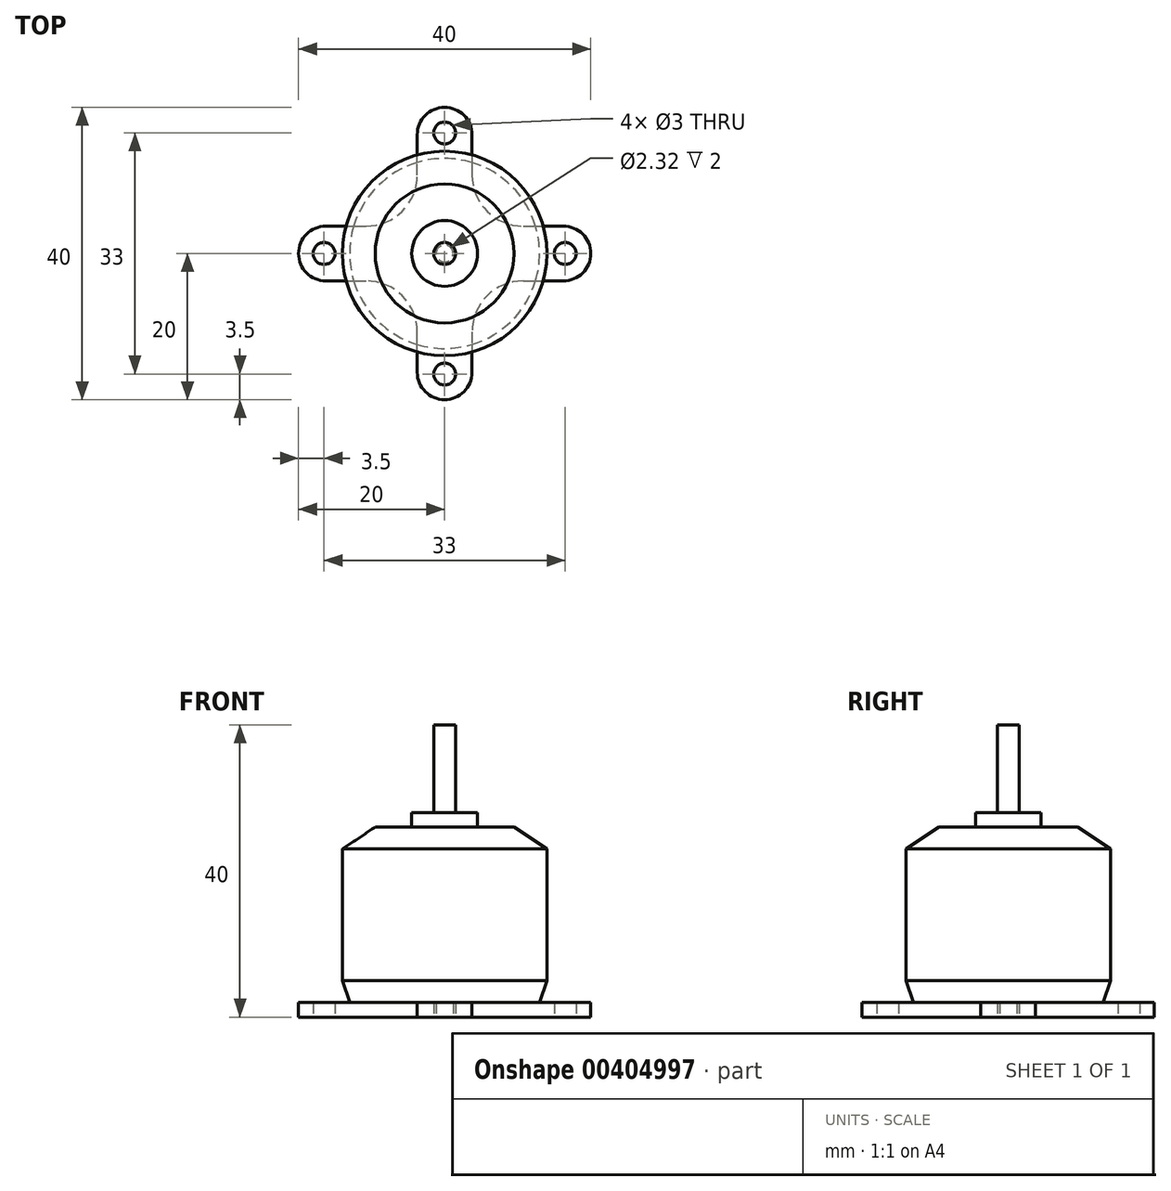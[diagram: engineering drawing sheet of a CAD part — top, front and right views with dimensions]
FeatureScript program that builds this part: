
annotation { "Feature Type Name" : "Feature", "Feature Type Description" : "" }
export const myFeature = defineFeature(function(context is Context, id is Id, definition is map)
    precondition{}
    {
        {
            var Q0;
            Q0=qCreatedBy(makeId("Front.planeOp"),FACE);
            var sketch = newSketch(context, id + "F0", { "sketchPlane" : qUnion([Q0])});
            skLineSegment(sketch, "E0", {"start": v(0, 0) * mm, "end": v(0, 40) * mm});
            skLineSegment(sketch, "E1", {"start": v(0, 40) * mm, "end": v(-1.5, 40) * mm});
            skLineSegment(sketch, "E2", {"start": v(-1.5, 40) * mm, "end": v(-1.5, 28) * mm});
            skLineSegment(sketch, "E3", {"start": v(-1.5, 28) * mm, "end": v(-4.5, 28) * mm});
            skLineSegment(sketch, "E4", {"start": v(-4.5, 28) * mm, "end": v(-4.5, 26) * mm});
            skLineSegment(sketch, "E5", {"start": v(-4.5, 26) * mm, "end": v(-9.5, 26) * mm});
            skLineSegment(sketch, "E6", {"start": v(-9.5, 26) * mm, "end": v(-14, 23) * mm});
            skLineSegment(sketch, "E7", {"start": v(-14, 23) * mm, "end": v(-14, 5) * mm});
            skLineSegment(sketch, "E8", {"start": v(-14, 5) * mm, "end": v(-13, 2) * mm});
            skLineSegment(sketch, "E9", {"start": v(-13, 2) * mm, "end": v(-20, 2) * mm});
            skLineSegment(sketch, "E10", {"start": v(-20, 2) * mm, "end": v(-20, 0) * mm});
            skLineSegment(sketch, "E11", {"start": v(-20, 0) * mm, "end": v(0, 0) * mm});
            skSolve(sketch);
        }
        {
            var Q0;
            Q0=makeQuery(id+"F0.imprint","IMPRINT",FACE,{"disambiguationData":[TD([[makeQuery(id+"F0.imprint","IMPRINT",EDGE,{"derivedFrom":sQuery(id+"F0.wireOp",EDGE,"E0")}),1.0]])]});
            var Q1;
            Q1=sQuery(id+"F0.wireOp",EDGE,"E0");
            revolve(context, id + "F1", {"entities" : qUnion([Q0]), "axis" : qUnion([Q1]), "revolveType" : RevolveType.FULL});
        }
        {
            var Q0;
            Q0=makeQuery(id+"F1.opRevolve","SWEPT_FACE",FACE,{"disambiguationData":[OSD([sQuery(id+"F0.wireOp",EDGE,"E11")])]});
            var sketch = newSketch(context, id + "F2", { "sketchPlane" : qUnion([Q0])});
            skLineSegment(sketch, "E12", {"start": v(0, 0) * mm, "end": v(0, 20) * mm, "construction": true});
            skLineSegment(sketch, "E13", {"start": v(0, 0) * mm, "end": v(0, -20) * mm, "construction": true});
            skLineSegment(sketch, "E14", {"start": v(0, 0) * mm, "end": v(-20, 0) * mm, "construction": true});
            skLineSegment(sketch, "E15", {"start": v(0, 0) * mm, "end": v(20, 0) * mm, "construction": true});
            skCircle(sketch, "E16", {"center": v(0, 16.25) * mm, "radius": 3.75 * mm});
            skCircle(sketch, "E17", {"center": v(16.25, 0) * mm, "radius": 3.75 * mm});
            skCircle(sketch, "E18", {"center": v(0, -16.25) * mm, "radius": 3.75 * mm});
            skCircle(sketch, "E19", {"center": v(-16.25, 0) * mm, "radius": 3.75 * mm});
            skLineSegment(sketch, "E20", {"start": v(0, 16.25) * mm, "end": v(-3.75, 16.25) * mm, "construction": true});
            skLineSegment(sketch, "E21", {"start": v(-3.75, 16.25) * mm, "end": v(-3.75, 0) * mm});
            skLineSegment(sketch, "E22", {"start": v(-3.75, 0) * mm, "end": v(-3.75, -16.25) * mm});
            skLineSegment(sketch, "E23", {"start": v(-16.25, 0) * mm, "end": v(-16.25, 3.75) * mm, "construction": true});
            skLineSegment(sketch, "E24", {"start": v(-16.25, 3.75) * mm, "end": v(16.25, 3.75) * mm});
            skLineSegment(sketch, "E25", {"start": v(-16.25, 0) * mm, "end": v(-16.25, -3.75) * mm, "construction": true});
            skLineSegment(sketch, "E26", {"start": v(-16.25, -3.75) * mm, "end": v(16.25, -3.75) * mm});
            skLineSegment(sketch, "E27", {"start": v(0, -16.25) * mm, "end": v(3.75, -16.25) * mm, "construction": true});
            skLineSegment(sketch, "E28", {"start": v(3.75, -16.25) * mm, "end": v(3.75, 16.25) * mm});
            skCircle(sketch, "E29", {"center": v(-16.25, 0) * mm, "radius": 1.5 * mm});
            skCircle(sketch, "E30", {"center": v(0, 16.25) * mm, "radius": 1.5 * mm});
            skCircle(sketch, "E31", {"center": v(16.25, 0) * mm, "radius": 1.5 * mm});
            skCircle(sketch, "E32", {"center": v(0, -16.25) * mm, "radius": 1.5 * mm});
            skCircle(sketch, "E33", {"center": v(0, 0) * mm, "radius": 1.16 * mm});
            skSolve(sketch);
        }
        {
            var Q0;
            {var subQ0=sQuery(id+"F2.wireOp",EDGE,"E24");var subQ3=sQuery(id+"F2.wireOp",EDGE,"E21");var subQ4=makeQuery(id+"F2.imprint","INTERSECT",VERTEX,{"derivedFrom":[subQ3,subQ0]});Q0=makeQuery(id+"F2.imprint","IMPRINT",FACE,{"disambiguationData":[TD([[makeQuery(id+"F2.imprint","IMPRINT",EDGE,{"disambiguationData":[TD([[subQ4,1.0]])],"derivedFrom":subQ3}),-1.0]])]});}
            var Q1;
            {var subQ0=sQuery(id+"F2.wireOp",EDGE,"E24");var subQ1=sQuery(id+"F2.wireOp",EDGE,"E17");var subQ2=makeQuery(id+"F2.imprint","INTERSECT",VERTEX,{"derivedFrom":[subQ1,subQ0]});Q1=makeQuery(id+"F2.imprint","IMPRINT",FACE,{"disambiguationData":[TD([[makeQuery(id+"F2.imprint","IMPRINT",EDGE,{"disambiguationData":[TD([[subQ2,1.0]])],"derivedFrom":subQ0}),1.0]])]});}
            var Q2;
            {var subQ3=sQuery(id+"F2.wireOp",EDGE,"E26");var subQ7=sQuery(id+"F2.wireOp",EDGE,"E17");var subQ8=makeQuery(id+"F2.imprint","INTERSECT",VERTEX,{"derivedFrom":[subQ7,subQ3]});Q2=makeQuery(id+"F2.imprint","IMPRINT",FACE,{"disambiguationData":[TD([[makeQuery(id+"F2.imprint","IMPRINT",EDGE,{"disambiguationData":[TD([[subQ8,1.0]])],"derivedFrom":subQ3}),-1.0]])]});}
            var Q3;
            {var subQ3=sQuery(id+"F2.wireOp",EDGE,"E22");var subQ5=sQuery(id+"F2.wireOp",EDGE,"E18");var subQ6=makeQuery(id+"F2.imprint","INTERSECT",VERTEX,{"derivedFrom":[subQ5,subQ3]});Q3=makeQuery(id+"F2.imprint","IMPRINT",FACE,{"disambiguationData":[TD([[makeQuery(id+"F2.imprint","IMPRINT",EDGE,{"disambiguationData":[TD([[subQ6,1.0]])],"derivedFrom":subQ3}),-1.0]])]});}
            extrude(context, id + "F3", {"entities" : qUnion([Q0, Q1, Q2, Q3]), "operationType" : NewBodyOperationType.REMOVE, "oppositeDirection" : true, "depth" : 2 * mm});
        }
        {
            var Q0;
            Q0=makeQuery(id+"F3.boolean.opBoolean","COPY",EDGE,{"derivedFrom":makeQuery(id+"F3.opExtrude","SWEPT_EDGE",EDGE,{"disambiguationData":[OSD([sQuery(id+"F2.wireOp",EDGE,"E26"),sQuery(id+"F2.wireOp",EDGE,"E28")])]})});
            var Q1;
            Q1=makeQuery(id+"F3.boolean.opBoolean","COPY",EDGE,{"derivedFrom":makeQuery(id+"F3.opExtrude","SWEPT_EDGE",EDGE,{"disambiguationData":[OSD([sQuery(id+"F2.wireOp",EDGE,"E22"),sQuery(id+"F2.wireOp",EDGE,"E26")])]})});
            var Q2;
            Q2=makeQuery(id+"F3.boolean.opBoolean","COPY",EDGE,{"derivedFrom":makeQuery(id+"F3.opExtrude","SWEPT_EDGE",EDGE,{"disambiguationData":[OSD([sQuery(id+"F2.wireOp",EDGE,"E21"),sQuery(id+"F2.wireOp",EDGE,"E24")])]})});
            var Q3;
            Q3=makeQuery(id+"F3.boolean.opBoolean","COPY",EDGE,{"derivedFrom":makeQuery(id+"F3.opExtrude","SWEPT_EDGE",EDGE,{"disambiguationData":[OSD([sQuery(id+"F2.wireOp",EDGE,"E24"),sQuery(id+"F2.wireOp",EDGE,"E28")])]})});
            fillet(context, id + "F4", {"entities" : qUnion([Q0, Q1, Q2, Q3]), "radius" : 7 * mm, "tangentPropagation" : true, "allowEdgeOverflow" : false});
        }
        {
            var Q0;
            Q0=makeQuery(id+"F2.imprint","IMPRINT",FACE,{"disambiguationData":[TD([[makeQuery(id+"F2.imprint","IMPRINT",EDGE,{"derivedFrom":sQuery(id+"F2.wireOp",EDGE,"E33")}),1.0]])]});
            extrude(context, id + "F5", {"entities" : qUnion([Q0]), "operationType" : NewBodyOperationType.REMOVE, "oppositeDirection" : true, "depth" : 2 * mm});
        }
        {
            var Q0;
            Q0=makeQuery(id+"F1.opRevolve","SWEPT_FACE",FACE,{"disambiguationData":[OSD([sQuery(id+"F0.wireOp",EDGE,"E11")])]});
            var sketch = newSketch(context, id + "F6", { "sketchPlane" : qUnion([Q0])});
            skLineSegment(sketch, "E34", {"start": v(0, 0) * mm, "end": v(0, 16.5) * mm});
            skLineSegment(sketch, "E35", {"start": v(0, 0) * mm, "end": v(16.5, 0) * mm});
            skLineSegment(sketch, "E36", {"start": v(0, 0) * mm, "end": v(0, -16.5) * mm});
            skLineSegment(sketch, "E37", {"start": v(0, 0) * mm, "end": v(-16.5, 0) * mm});
            skCircle(sketch, "E38", {"center": v(0, 16.5) * mm, "radius": 1.5 * mm});
            skCircle(sketch, "E39", {"center": v(16.5, 0) * mm, "radius": 1.5 * mm});
            skCircle(sketch, "E40", {"center": v(0, -16.5) * mm, "radius": 1.5 * mm});
            skCircle(sketch, "E41", {"center": v(-16.5, 0) * mm, "radius": 1.5 * mm});
            skPoint(sketch, "E42", {"position": v(0, 15) * mm});
            skSolve(sketch);
        }
        {
            var Q0;
            Q0=makeQuery(id+"F6.imprint","IMPRINT",FACE,{"disambiguationData":[TD([[makeQuery(id+"F6.imprint","IMPRINT",EDGE,{"derivedFrom":sQuery(id+"F6.wireOp",EDGE,"E38")}),1.0]])]});
            var Q1;
            Q1=makeQuery(id+"F6.imprint","IMPRINT",FACE,{"disambiguationData":[TD([[makeQuery(id+"F6.imprint","IMPRINT",EDGE,{"derivedFrom":sQuery(id+"F6.wireOp",EDGE,"E41")}),1.0]])]});
            var Q2;
            Q2=makeQuery(id+"F6.imprint","IMPRINT",FACE,{"disambiguationData":[TD([[makeQuery(id+"F6.imprint","IMPRINT",EDGE,{"derivedFrom":sQuery(id+"F6.wireOp",EDGE,"E40")}),1.0]])]});
            var Q3;
            Q3=makeQuery(id+"F6.imprint","IMPRINT",FACE,{"disambiguationData":[TD([[makeQuery(id+"F6.imprint","IMPRINT",EDGE,{"derivedFrom":sQuery(id+"F6.wireOp",EDGE,"E39")}),1.0]])]});
            extrude(context, id + "F7", {"entities" : qUnion([Q0, Q1, Q2, Q3]), "operationType" : NewBodyOperationType.REMOVE, "oppositeDirection" : true, "depth" : 2 * mm});
        }
    });
